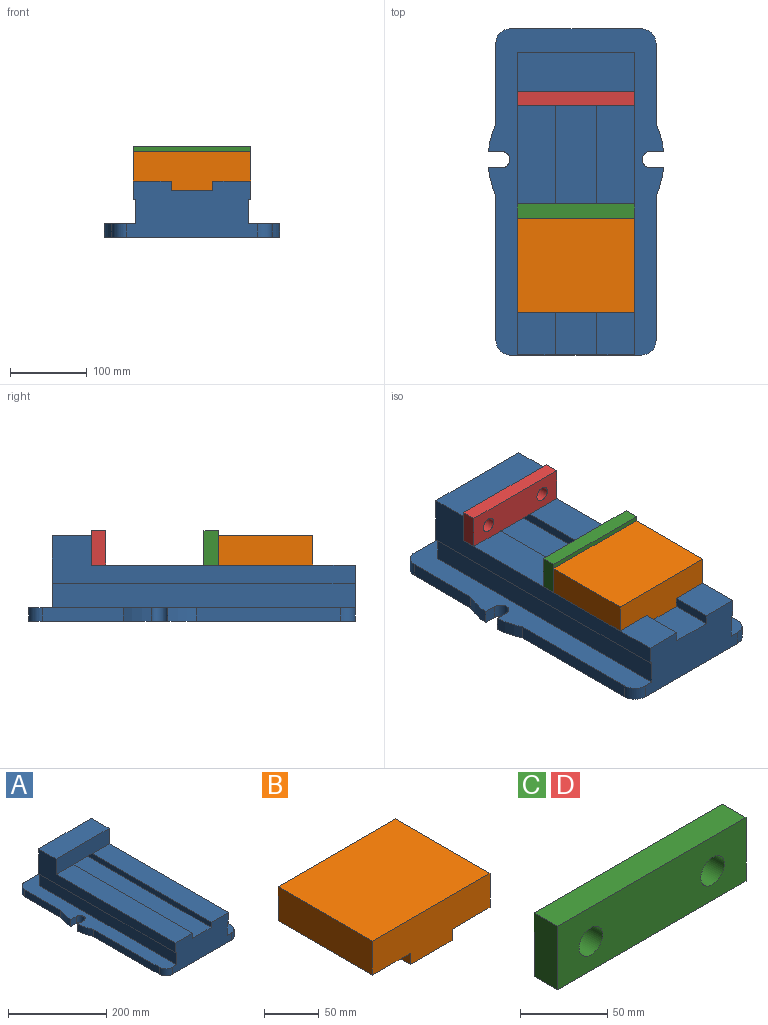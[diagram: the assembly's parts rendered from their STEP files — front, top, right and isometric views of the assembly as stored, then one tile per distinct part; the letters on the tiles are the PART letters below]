
ASSEMBLY  parts=4 mates=6
PART A: 37 faces, bbox 227.6x423.9x111.1 mm
  f0: plane 187.5x17.46mm, normal (1,0,0), area 3274.3mm2, adj f1,f18,f19,f21
  f1: cylinder r=114.3mm len=36.77mm, axis (0,0,-1), area 667.7mm2, adj f0,f2,f18,f21
  f2: plane 17.46x16.96mm, normal (0,1,0), area 296.2mm2, adj f1,f3,f18,f21
  f3: cylinder r=10.67mm len=21.35mm, axis (0,0,-1), area 585.5mm2, adj f2,f4,f18,f21
  f4: plane 17.46x16.96mm, normal (0,-1,0), area 296.2mm2, adj f3,f5,f18,f21
  f5: cylinder r=114.3mm len=36.77mm, axis (0,0,-1), area 667.7mm2, adj f4,f6,f18,f21
  f6: plane 103.37x17.46mm, normal (1,0,0), area 1805mm2, adj f5,f7,f18,f21
  f7: cylinder r=19.05mm len=19.05mm, axis (0,0,-1), area 522.5mm2, adj f6,f8,f18,f21
  f8: plane 171.12x17.46mm, normal (0,1,0), area 2988.2mm2, adj f7,f9,f18,f21
  f9: cylinder r=17.81mm len=17.81mm, axis (0,0,-1), area 488.4mm2, adj f8,f10,f18,f21
  f10: plane 104.61x17.46mm, normal (-1,0,0), area 1826.8mm2, adj f9,f11,f18,f21
  f11: cylinder r=114.3mm len=36.77mm, axis (0,0,-1), area 667.7mm2, adj f10,f12,f18,f21
  f12: plane 17.46x16.96mm, normal (0,-1,0), area 296.2mm2, adj f11,f13,f18,f21
  f13: cylinder r=10.67mm len=21.35mm, axis (0,0,-1), area 585.5mm2, adj f12,f14,f18,f21
  f14: plane 17.46x16.96mm, normal (0,1,0), area 296.2mm2, adj f13,f15,f18,f21
  f15: cylinder r=114.3mm len=36.77mm, axis (0,0,-1), area 667.7mm2, adj f14,f16,f18,f21
  f16: plane 187.5x17.46mm, normal (-1,0,0), area 3274.3mm2, adj f15,f17,f18,f21
  f17: cylinder r=19.05mm len=19.05mm, axis (0,0,-1), area 522.5mm2, adj f16,f18,f21,f27
  f18: plane 423.86x227.6mm, normal (0,0,-1), area 88071.8mm2, adj f0,f1,f2,f3,f4,f5,f6,f7
  f19: cylinder r=19.05mm len=19.05mm, axis (0,0,-1), area 522.5mm2, adj f0,f18,f21,f27
  f20: plane 393.7x31.75mm, normal (1,0,0), area 12500mm2, adj f21,f27,f28,f29
  f21: plane 423.86x227.6mm, normal (0,0,1), area 30572mm2, adj f0,f1,f2,f3,f4,f5,f6,f7
  f22: plane 393.7x31.75mm, normal (-1,0,0), area 12500mm2, adj f21,f24,f27,f29
  f23: plane 393.7x53.98mm, normal (0,0,1), area 21250mm2, adj f25,f26,f27,f29
  f24: plane 393.7x3.18mm, normal (0,0,-1), area 1250mm2, adj f22,f27,f29,f31
  f25: plane 393.7x12.7mm, normal (1,0,0), area 5000mm2, adj f23,f27,f29,f32,f33
  f26: plane 393.7x12.7mm, normal (-1,0,0), area 5000mm2, adj f23,f27,f29,f33,f34
  f27: plane 169.88x73.03mm, normal (0,-1,0), area 10547.1mm2, adj f17,f18,f19,f20,f21,f22,f23,f24
  f28: plane 393.7x3.18mm, normal (0,0,-1), area 1250mm2, adj f20,f27,f29,f35
  f29: plane 152.4x93.66mm, normal (0,1,0), area 13387.1mm2, adj f20,f21,f22,f23,f24,f25,f26,f28
  f30: plane 152.4x50.8mm, normal (0,0,1), area 7741.9mm2, adj f29,f31,f35,f36
  f31: plane 393.7x61.91mm, normal (-1,0,0), area 11310.5mm2, adj f24,f27,f29,f30,f32,f36
  f32: plane 342.9x49.21mm, normal (0,0,1), area 16875mm2, adj f25,f27,f31,f36
  f33: plane 53.98x50.8mm, normal (0,0,-1), area 2741.9mm2, adj f25,f26,f29,f36
  f34: plane 342.9x49.21mm, normal (0,0,1), area 16875mm2, adj f26,f27,f35,f36
  f35: plane 393.7x61.91mm, normal (1,0,0), area 11310.5mm2, adj f27,f28,f29,f30,f34,f36
  f36: plane 152.4x38.1mm, normal (0,-1,0), area 5806.4mm2, adj f30,f31,f32,f33,f34,f35
PART B: 10 faces, bbox 152.4x122.2x50.8 mm
  f0: plane 152.4x122.24mm, normal (0,0,1), area 18629mm2, adj f1,f4,f6,f8
  f1: plane 122.24x38.1mm, normal (1,0,0), area 4657.2mm2, adj f0,f2,f6,f8
  f2: plane 122.24x49.21mm, normal (0,0,-1), area 6015.6mm2, adj f1,f3,f6,f8
  f3: plane 122.24x12.7mm, normal (1,0,0), area 1552.4mm2, adj f2,f5,f6,f8
  f4: plane 122.24x38.1mm, normal (-1,0,0), area 4657.2mm2, adj f0,f6,f7,f8
  f5: plane 122.24x53.98mm, normal (0,0,-1), area 6597.8mm2, adj f3,f6,f8,f9
  f6: plane 152.4x50.8mm, normal (0,-1,0), area 6491.9mm2, adj f0,f1,f2,f3,f4,f5,f7,f9
  f7: plane 122.24x49.21mm, normal (0,0,-1), area 6015.6mm2, adj f4,f6,f8,f9
  f8: plane 152.4x50.8mm, normal (0,1,0), area 6491.9mm2, adj f0,f1,f2,f3,f4,f5,f7,f9
  f9: plane 122.24x12.7mm, normal (-1,0,0), area 1552.4mm2, adj f5,f6,f7,f8
PART C: 8 faces, bbox 152.4x19.1x44.5 mm
  f0: cylinder r=9.53mm len=19.05mm, axis (0,1,0), area 1140.1mm2, adj f3,f5
  f1: cylinder r=9.53mm len=19.05mm, axis (0,1,0), area 1140.1mm2, adj f3,f5
  f2: plane 152.4x19.05mm, normal (0,0,1), area 2903.2mm2, adj f3,f4,f5,f6
  f3: plane 152.4x44.45mm, normal (0,1,0), area 6204.1mm2, adj f0,f1,f2,f4,f6,f7
  f4: plane 44.45x19.05mm, normal (1,0,0), area 846.8mm2, adj f2,f3,f5,f7
  f5: plane 152.4x44.45mm, normal (0,-1,0), area 6204.1mm2, adj f0,f1,f2,f4,f6,f7
  f6: plane 44.45x19.05mm, normal (-1,0,0), area 846.8mm2, adj f2,f3,f5,f7
  f7: plane 152.4x19.05mm, normal (0,0,-1), area 2903.2mm2, adj f3,f4,f5,f6
PART D: same geometry as C
PLACE A t=(0,-146.05,-61.91)mm
PLACE B t=(0,-165.58,-38.1)mm
PLACE C t=(0,-156.06,-38.1)mm
PLACE D t=(0,-9.53,-38.1)mm
MATE planar A.f35 <-> C.f4  axis (1,0,0) through (76.2,-116.71,-44.71)mm
MATE planar C.f5 <-> B.f8  axis (0,-1,0) through (0,-165.58,-15.73)mm
MATE planar C.f7 <-> A.f34  axis (0,0,-1) through (0,-156.06,-38.1)mm
MATE planar A.f32 <-> B.f7  axis (0,0,1) through (-51.59,-171.45,-38.1)mm
MATE fastened D.f7 <-> A.f33  axis (0,0,1) through (0,0,-38.1)mm
MATE planar B.f3 <-> A.f26  axis (1,0,0) through (26.99,-226.7,-44.45)mm
